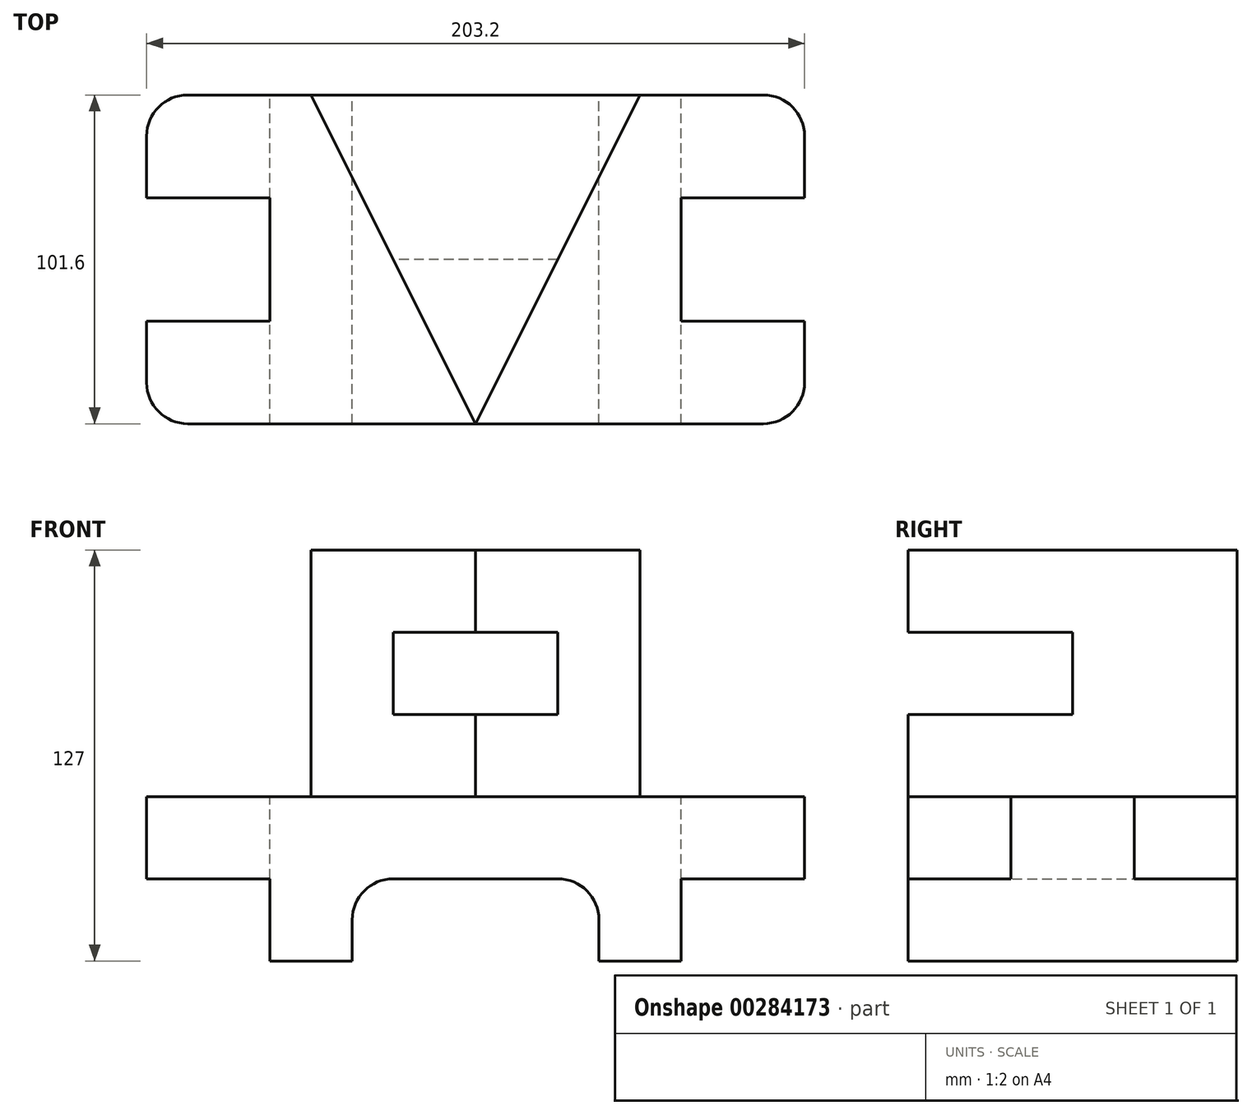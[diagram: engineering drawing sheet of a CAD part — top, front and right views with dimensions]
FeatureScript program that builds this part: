
annotation { "Feature Type Name" : "Feature", "Feature Type Description" : "" }
export const myFeature = defineFeature(function(context is Context, id is Id, definition is map)
    precondition{}
    {
        {
            var Q0;
            Q0=qCreatedBy(makeId("Front.planeOp"),FACE);
            var sketch = newSketch(context, id + "F0", { "sketchPlane" : qUnion([Q0])});
            skLineSegment(sketch, "E0.bottom", {"start": v(0, 0) * mm, "end": v(203.2, 0) * mm});
            skLineSegment(sketch, "E0.top", {"start": v(76.2, -25.4) * mm, "end": v(127, -25.4) * mm});
            skLineSegment(sketch, "E0.left", {"start": v(0, 0) * mm, "end": v(0, -25.4) * mm});
            skLineSegment(sketch, "E0.right", {"start": v(203.2, 0) * mm, "end": v(203.2, -25.4) * mm});
            skLineSegment(sketch, "E1.top", {"start": v(38.1, -50.8) * mm, "end": v(63.5, -50.8) * mm});
            skLineSegment(sketch, "E1.left", {"start": v(38.1, -25.4) * mm, "end": v(38.1, -50.8) * mm});
            skLineSegment(sketch, "E2.top", {"start": v(139.7, -50.8) * mm, "end": v(165.1, -50.8) * mm});
            skLineSegment(sketch, "E2.right", {"start": v(165.1, -25.4) * mm, "end": v(165.1, -50.8) * mm});
            skLineSegment(sketch, "E3", {"start": v(139.7, -50.8) * mm, "end": v(139.7, -38.1) * mm});
            skArc(sketch, "E4.filletArc", {"start": v(139.7, -38.1) * mm, "mid": v(135.98, -29.12) * mm, "end": v(127, -25.4) * mm});
            skLineSegment(sketch, "E5", {"start": v(63.5, -50.8) * mm, "end": v(63.5, -38.1) * mm});
            skArc(sketch, "E6.filletArc", {"start": v(76.2, -25.4) * mm, "mid": v(67.22, -29.12) * mm, "end": v(63.5, -38.1) * mm});
            skLineSegment(sketch, "E7", {"start": v(0, -25.4) * mm, "end": v(38.1, -25.4) * mm});
            skLineSegment(sketch, "E8", {"start": v(165.1, -25.4) * mm, "end": v(203.2, -25.4) * mm});
            skSolve(sketch);
        }
        {
            var Q0;
            Q0 = qSketchRegion(id + "F0", true);
            extrude(context, id + "F1", {"entities" : qUnion([Q0]), "depth" : 101.6 * mm});
        }
        {
            var Q0;
            Q0=qCreatedBy(makeId("Top.planeOp"),FACE);
            var sketch = newSketch(context, id + "F2", { "sketchPlane" : qUnion([Q0])});
            skLineSegment(sketch, "E9", {"start": v(50.8, 0) * mm, "end": v(101.6, -101.6) * mm});
            skLineSegment(sketch, "E10", {"start": v(101.6, -101.6) * mm, "end": v(152.4, 0) * mm});
            skLineSegment(sketch, "E11", {"start": v(152.4, 0) * mm, "end": v(50.8, 0) * mm});
            skSolve(sketch);
        }
        {
            var Q0;
            Q0 = qSketchRegion(id + "F2", true);
            extrude(context, id + "F3", {"entities" : qUnion([Q0]), "operationType" : NewBodyOperationType.ADD, "depth" : 76.2 * mm});
        }
        {
            var Q0;
            Q0=qCreatedBy(makeId("Right.planeOp"),FACE);
            var sketch = newSketch(context, id + "F4", { "sketchPlane" : qUnion([Q0])});
            skLineSegment(sketch, "E12.bottom", {"start": v(-101.6, 50.8) * mm, "end": v(-50.8, 50.8) * mm});
            skLineSegment(sketch, "E12.top", {"start": v(-101.6, 25.4) * mm, "end": v(-50.8, 25.4) * mm});
            skLineSegment(sketch, "E12.left", {"start": v(-101.6, 50.8) * mm, "end": v(-101.6, 25.4) * mm});
            skLineSegment(sketch, "E12.right", {"start": v(-50.8, 50.8) * mm, "end": v(-50.8, 25.4) * mm});
            skSolve(sketch);
        }
        {
            var Q0;
            Q0 = qSketchRegion(id + "F4", true);
            extrude(context, id + "F5", {"entities" : qUnion([Q0]), "operationType" : NewBodyOperationType.REMOVE, "endBound" : BoundingType.THROUGH_ALL, "depth" : 25.4 * mm});
        }
        {
            var Q0;
            Q0=qCreatedBy(makeId("Top.planeOp"),FACE);
            var sketch = newSketch(context, id + "F6", { "sketchPlane" : qUnion([Q0])});
            skLineSegment(sketch, "E13.bottom", {"start": v(0, -31.75) * mm, "end": v(38.1, -31.75) * mm});
            skLineSegment(sketch, "E13.top", {"start": v(0, -69.85) * mm, "end": v(38.1, -69.85) * mm});
            skLineSegment(sketch, "E13.left", {"start": v(0, -31.75) * mm, "end": v(0, -69.85) * mm});
            skLineSegment(sketch, "E13.right", {"start": v(38.1, -31.75) * mm, "end": v(38.1, -69.85) * mm});
            skLineSegment(sketch, "E14.bottom", {"start": v(203.2, -31.75) * mm, "end": v(165.1, -31.75) * mm});
            skLineSegment(sketch, "E14.top", {"start": v(203.2, -69.85) * mm, "end": v(165.1, -69.85) * mm});
            skLineSegment(sketch, "E14.left", {"start": v(203.2, -31.75) * mm, "end": v(203.2, -69.85) * mm});
            skLineSegment(sketch, "E14.right", {"start": v(165.1, -31.75) * mm, "end": v(165.1, -69.85) * mm});
            skSolve(sketch);
        }
        {
            var Q0;
            Q0 = qSketchRegion(id + "F6", true);
            extrude(context, id + "F7", {"entities" : qUnion([Q0]), "operationType" : NewBodyOperationType.REMOVE, "endBound" : BoundingType.THROUGH_ALL, "oppositeDirection" : true, "depth" : 25.4 * mm});
        }
        {
            var Q0;
            Q0=makeQuery(id+"F1.opExtrude","CAP_EDGE",EDGE,{"disambiguationData":[OSD([sQuery(id+"F0.wireOp",EDGE,"E0.left")])],"isStart":false});
            var Q1;
            Q1=makeQuery(id+"F1.opExtrude","CAP_EDGE",EDGE,{"disambiguationData":[OSD([sQuery(id+"F0.wireOp",EDGE,"E0.left")])],"isStart":true});
            var Q2;
            Q2=makeQuery(id+"F1.opExtrude","CAP_EDGE",EDGE,{"disambiguationData":[OSD([sQuery(id+"F0.wireOp",EDGE,"E0.right")])],"isStart":true});
            var Q3;
            Q3=makeQuery(id+"F1.opExtrude","CAP_EDGE",EDGE,{"disambiguationData":[OSD([sQuery(id+"F0.wireOp",EDGE,"E0.right")])],"isStart":false});
            fillet(context, id + "F8", {"entities" : qUnion([Q0, Q1, Q2, Q3]), "radius" : 12.7 * mm, "tangentPropagation" : true, "allowEdgeOverflow" : false});
        }
    });
